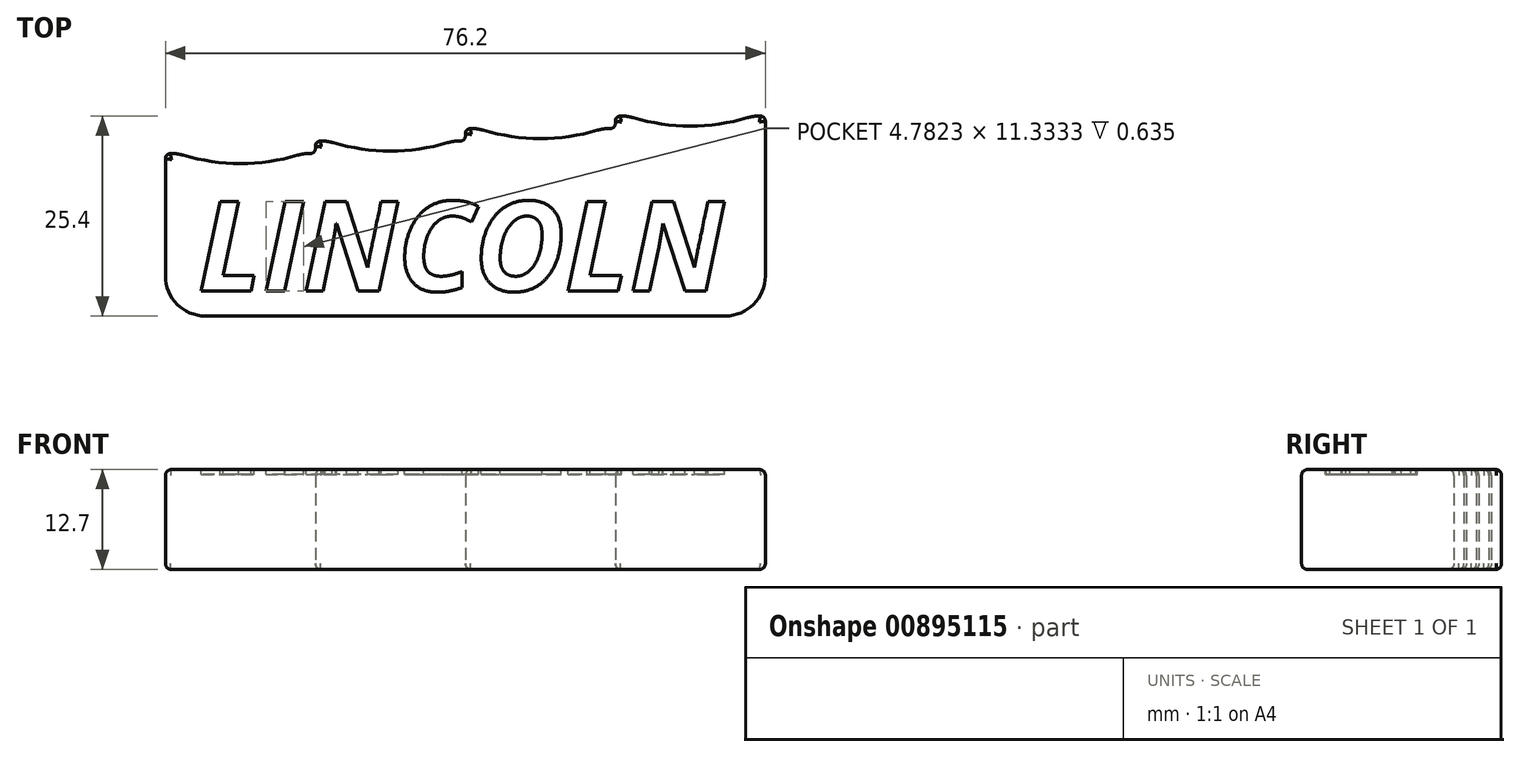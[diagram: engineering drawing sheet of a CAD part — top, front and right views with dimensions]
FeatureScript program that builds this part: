
annotation { "Feature Type Name" : "Feature", "Feature Type Description" : "" }
export const myFeature = defineFeature(function(context is Context, id is Id, definition is map)
    precondition{}
    {
        {
            var Q0;
            Q0=qCreatedBy(makeId("Top.planeOp"),FACE);
            var sketch = newSketch(context, id + "F0", { "sketchPlane" : qUnion([Q0])});
            skLineSegment(sketch, "E0", {"start": v(0, 0) * mm, "end": v(76.2, 0) * mm});
            skLineSegment(sketch, "E1", {"start": v(0, 0) * mm, "end": v(0, 20.64) * mm});
            skLineSegment(sketch, "E2", {"start": v(0, 20.64) * mm, "end": v(1.6, 20.64) * mm});
            skLineSegment(sketch, "E3", {"start": v(19.05, 20.64) * mm, "end": v(19.05, 22.23) * mm});
            skLineSegment(sketch, "E4", {"start": v(19.05, 22.23) * mm, "end": v(20.64, 22.23) * mm});
            skLineSegment(sketch, "E5", {"start": v(38.1, 22.23) * mm, "end": v(38.1, 23.81) * mm});
            skLineSegment(sketch, "E6", {"start": v(38.1, 23.81) * mm, "end": v(39.7, 23.81) * mm});
            skLineSegment(sketch, "E7", {"start": v(57.15, 23.81) * mm, "end": v(57.15, 25.4) * mm});
            skLineSegment(sketch, "E8", {"start": v(57.15, 25.4) * mm, "end": v(58.74, 25.4) * mm});
            skLineSegment(sketch, "E9", {"start": v(76.2, 25.4) * mm, "end": v(76.2, 0) * mm});
            skArc(sketch, "E10", {"start": v(1.6, 20.64) * mm, "mid": v(9.52, 19.37) * mm, "end": v(17.46, 20.64) * mm});
            skArc(sketch, "E11", {"start": v(20.64, 22.23) * mm, "mid": v(28.58, 20.95) * mm, "end": v(36.5, 22.23) * mm});
            skArc(sketch, "E12", {"start": v(58.74, 25.4) * mm, "mid": v(66.68, 24.13) * mm, "end": v(74.6, 25.4) * mm});
            skArc(sketch, "E13", {"start": v(39.7, 23.81) * mm, "mid": v(47.62, 22.54) * mm, "end": v(55.56, 23.81) * mm});
            skLineSegment(sketch, "E14.trimOffspring", {"start": v(17.46, 20.64) * mm, "end": v(19.05, 20.64) * mm});
            skPoint(sketch, "E15.end.orphan", {"position": v(9.53, 20.64) * mm});
            skPoint(sketch, "E15.start.orphan", {"position": v(9.52, 19.37) * mm});
            skLineSegment(sketch, "E16.trimOffspring", {"start": v(36.5, 22.23) * mm, "end": v(38.1, 22.23) * mm});
            skPoint(sketch, "E17.start.orphan", {"position": v(28.58, 20.95) * mm});
            skPoint(sketch, "E18.orphan", {"position": v(28.58, 22.23) * mm});
            skLineSegment(sketch, "E19.trimOffspring", {"start": v(55.56, 23.81) * mm, "end": v(57.15, 23.81) * mm});
            skPoint(sketch, "E20.start.orphan", {"position": v(47.62, 22.54) * mm});
            skPoint(sketch, "E21.orphan", {"position": v(47.62, 23.81) * mm});
            skLineSegment(sketch, "E22.trimOffspring", {"start": v(74.6, 25.4) * mm, "end": v(76.2, 25.4) * mm});
            skPoint(sketch, "E23.start.orphan", {"position": v(66.68, 24.13) * mm});
            skPoint(sketch, "E24.orphan", {"position": v(66.68, 25.4) * mm});
            skSolve(sketch);
        }
        {
            var Q0;
            Q0 = qSketchRegion(id + "F0", true);
            extrude(context, id + "F1", {"entities" : qUnion([Q0]), "depth" : 12.7 * mm, "offsetDistance" : 25.4 * mm});
        }
        {
            var Q0;
            Q0=makeQuery(id+"F1.opExtrude","SWEPT_EDGE",EDGE,{"disambiguationData":[OSD([sQuery(id+"F0.wireOp",EDGE,"E1"),sQuery(id+"F0.wireOp",EDGE,"E2")])]});
            var Q1;
            Q1=makeQuery(id+"F1.opExtrude","SWEPT_EDGE",EDGE,{"disambiguationData":[OSD([sQuery(id+"F0.wireOp",EDGE,"E3"),sQuery(id+"F0.wireOp",EDGE,"E4")])]});
            var Q2;
            Q2=makeQuery(id+"F1.opExtrude","SWEPT_EDGE",EDGE,{"disambiguationData":[OSD([sQuery(id+"F0.wireOp",EDGE,"E3"),sQuery(id+"F0.wireOp",EDGE,"E14.trimOffspring")])]});
            var Q3;
            Q3=makeQuery(id+"F1.opExtrude","SWEPT_EDGE",EDGE,{"disambiguationData":[OSD([sQuery(id+"F0.wireOp",EDGE,"E5"),sQuery(id+"F0.wireOp",EDGE,"E16.trimOffspring")])]});
            var Q4;
            Q4=makeQuery(id+"F1.opExtrude","SWEPT_EDGE",EDGE,{"disambiguationData":[OSD([sQuery(id+"F0.wireOp",EDGE,"E5"),sQuery(id+"F0.wireOp",EDGE,"E6")])]});
            var Q5;
            Q5=makeQuery(id+"F1.opExtrude","SWEPT_EDGE",EDGE,{"disambiguationData":[OSD([sQuery(id+"F0.wireOp",EDGE,"E7"),sQuery(id+"F0.wireOp",EDGE,"E19.trimOffspring")])]});
            var Q6;
            Q6=makeQuery(id+"F1.opExtrude","SWEPT_EDGE",EDGE,{"disambiguationData":[OSD([sQuery(id+"F0.wireOp",EDGE,"E7"),sQuery(id+"F0.wireOp",EDGE,"E8")])]});
            var Q7;
            Q7=makeQuery(id+"F1.opExtrude","SWEPT_EDGE",EDGE,{"disambiguationData":[OSD([sQuery(id+"F0.wireOp",EDGE,"E9"),sQuery(id+"F0.wireOp",EDGE,"E22.trimOffspring")])]});
            fillet(context, id + "F2", {"entities" : qUnion([Q0, Q1, Q2, Q3, Q4, Q5, Q6, Q7]), "radius" : 0.64 * mm, "tangentPropagation" : true, "allowEdgeOverflow" : false});
        }
        {
            var Q0;
            Q0=makeQuery(id+"F1.opExtrude","SWEPT_EDGE",EDGE,{"disambiguationData":[OSD([sQuery(id+"F0.wireOp",EDGE,"E10"),sQuery(id+"F0.wireOp",EDGE,"E14.trimOffspring")])]});
            var Q1;
            Q1=makeQuery(id+"F1.opExtrude","SWEPT_EDGE",EDGE,{"disambiguationData":[OSD([sQuery(id+"F0.wireOp",EDGE,"E2"),sQuery(id+"F0.wireOp",EDGE,"E10")])]});
            var Q2;
            Q2=makeQuery(id+"F1.opExtrude","SWEPT_EDGE",EDGE,{"disambiguationData":[OSD([sQuery(id+"F0.wireOp",EDGE,"E4"),sQuery(id+"F0.wireOp",EDGE,"E11")])]});
            var Q3;
            Q3=makeQuery(id+"F1.opExtrude","SWEPT_EDGE",EDGE,{"disambiguationData":[OSD([sQuery(id+"F0.wireOp",EDGE,"E6"),sQuery(id+"F0.wireOp",EDGE,"E13")])]});
            var Q4;
            Q4=makeQuery(id+"F1.opExtrude","SWEPT_EDGE",EDGE,{"disambiguationData":[OSD([sQuery(id+"F0.wireOp",EDGE,"E11"),sQuery(id+"F0.wireOp",EDGE,"E16.trimOffspring")])]});
            var Q5;
            Q5=makeQuery(id+"F1.opExtrude","SWEPT_EDGE",EDGE,{"disambiguationData":[OSD([sQuery(id+"F0.wireOp",EDGE,"E8"),sQuery(id+"F0.wireOp",EDGE,"E12")])]});
            var Q6;
            Q6=makeQuery(id+"F1.opExtrude","SWEPT_EDGE",EDGE,{"disambiguationData":[OSD([sQuery(id+"F0.wireOp",EDGE,"E13"),sQuery(id+"F0.wireOp",EDGE,"E19.trimOffspring")])]});
            var Q7;
            Q7=makeQuery(id+"F1.opExtrude","SWEPT_EDGE",EDGE,{"disambiguationData":[OSD([sQuery(id+"F0.wireOp",EDGE,"E12"),sQuery(id+"F0.wireOp",EDGE,"E22.trimOffspring")])]});
            fillet(context, id + "F3", {"entities" : qUnion([Q0, Q1, Q2, Q3, Q4, Q5, Q6, Q7]), "radius" : 5.08 * mm, "tangentPropagation" : true, "allowEdgeOverflow" : false});
        }
        {
            var Q0;
            Q0=makeQuery(id+"F1.opExtrude","CAP_FACE",FACE,{"disambiguationData":[OSD([sQuery(id+"F0.wireOp",EDGE,"E0"),sQuery(id+"F0.wireOp",EDGE,"E1"),sQuery(id+"F0.wireOp",EDGE,"E2"),sQuery(id+"F0.wireOp",EDGE,"E3"),sQuery(id+"F0.wireOp",EDGE,"E4"),sQuery(id+"F0.wireOp",EDGE,"E5"),sQuery(id+"F0.wireOp",EDGE,"E6"),sQuery(id+"F0.wireOp",EDGE,"E7"),sQuery(id+"F0.wireOp",EDGE,"E8"),sQuery(id+"F0.wireOp",EDGE,"E9"),sQuery(id+"F0.wireOp",EDGE,"E10"),sQuery(id+"F0.wireOp",EDGE,"E11"),sQuery(id+"F0.wireOp",EDGE,"E12"),sQuery(id+"F0.wireOp",EDGE,"E13"),sQuery(id+"F0.wireOp",EDGE,"E14.trimOffspring"),sQuery(id+"F0.wireOp",EDGE,"E16.trimOffspring"),sQuery(id+"F0.wireOp",EDGE,"E19.trimOffspring"),sQuery(id+"F0.wireOp",EDGE,"E22.trimOffspring")])],"isStart":false});
            var sketch = newSketch(context, id + "F4", { "sketchPlane" : qUnion([Q0])});
            skText(sketch, "E25", { "text": "LINCOLN", "fontName": "OpenSans-BoldItalic.ttf"});
            skLineSegment(sketch, "E26", {"start": v(38.1, 0) * mm, "end": v(38.1, 3.17) * mm});
            const initialGuessF4  = {"E25": [0.00413, 0.00318, 1, 0, 0.01143]};
            skSetInitialGuess(sketch, initialGuessF4);
            skSolve(sketch);
        }
        {
            var Q0;
            Q0=makeQuery(id+"F1.opExtrude","SWEPT_EDGE",EDGE,{"disambiguationData":[OSD([sQuery(id+"F0.wireOp",EDGE,"E0"),sQuery(id+"F0.wireOp",EDGE,"E1")])]});
            var Q1;
            Q1=makeQuery(id+"F1.opExtrude","SWEPT_EDGE",EDGE,{"disambiguationData":[OSD([sQuery(id+"F0.wireOp",EDGE,"E0"),sQuery(id+"F0.wireOp",EDGE,"E9")])]});
            fillet(context, id + "F5", {"entities" : qUnion([Q0, Q1]), "radius" : 5.08 * mm, "tangentPropagation" : true, "allowEdgeOverflow" : false});
        }
        {
            var Q0;
            Q0=makeQuery(id+"F1.opExtrude","CAP_FACE",FACE,{"disambiguationData":[OSD([sQuery(id+"F0.wireOp",EDGE,"E0"),sQuery(id+"F0.wireOp",EDGE,"E1"),sQuery(id+"F0.wireOp",EDGE,"E2"),sQuery(id+"F0.wireOp",EDGE,"E3"),sQuery(id+"F0.wireOp",EDGE,"E4"),sQuery(id+"F0.wireOp",EDGE,"E5"),sQuery(id+"F0.wireOp",EDGE,"E6"),sQuery(id+"F0.wireOp",EDGE,"E7"),sQuery(id+"F0.wireOp",EDGE,"E8"),sQuery(id+"F0.wireOp",EDGE,"E9"),sQuery(id+"F0.wireOp",EDGE,"E10"),sQuery(id+"F0.wireOp",EDGE,"E11"),sQuery(id+"F0.wireOp",EDGE,"E12"),sQuery(id+"F0.wireOp",EDGE,"E13"),sQuery(id+"F0.wireOp",EDGE,"E14.trimOffspring"),sQuery(id+"F0.wireOp",EDGE,"E16.trimOffspring"),sQuery(id+"F0.wireOp",EDGE,"E19.trimOffspring"),sQuery(id+"F0.wireOp",EDGE,"E22.trimOffspring")])],"isStart":false});
            var Q1;
            Q1=makeQuery(id+"F1.opExtrude","CAP_FACE",FACE,{"disambiguationData":[OSD([sQuery(id+"F0.wireOp",EDGE,"E0"),sQuery(id+"F0.wireOp",EDGE,"E1"),sQuery(id+"F0.wireOp",EDGE,"E2"),sQuery(id+"F0.wireOp",EDGE,"E3"),sQuery(id+"F0.wireOp",EDGE,"E4"),sQuery(id+"F0.wireOp",EDGE,"E5"),sQuery(id+"F0.wireOp",EDGE,"E6"),sQuery(id+"F0.wireOp",EDGE,"E7"),sQuery(id+"F0.wireOp",EDGE,"E8"),sQuery(id+"F0.wireOp",EDGE,"E9"),sQuery(id+"F0.wireOp",EDGE,"E10"),sQuery(id+"F0.wireOp",EDGE,"E11"),sQuery(id+"F0.wireOp",EDGE,"E12"),sQuery(id+"F0.wireOp",EDGE,"E13"),sQuery(id+"F0.wireOp",EDGE,"E14.trimOffspring"),sQuery(id+"F0.wireOp",EDGE,"E16.trimOffspring"),sQuery(id+"F0.wireOp",EDGE,"E19.trimOffspring"),sQuery(id+"F0.wireOp",EDGE,"E22.trimOffspring")])],"isStart":true});
            fillet(context, id + "F6", {"entities" : qUnion([Q0, Q1]), "radius" : 0.76 * mm, "tangentPropagation" : true, "allowEdgeOverflow" : false});
        }
        {
            var Q0;
            Q0 = qSketchRegion(id + "F4", true);
            extrude(context, id + "F7", {"entities" : qUnion([Q0]), "operationType" : NewBodyOperationType.REMOVE, "oppositeDirection" : true, "depth" : 0.64 * mm, "offsetDistance" : 25.4 * mm});
        }
    });
